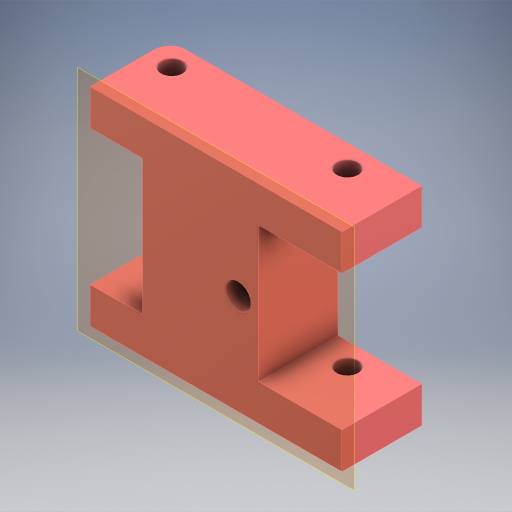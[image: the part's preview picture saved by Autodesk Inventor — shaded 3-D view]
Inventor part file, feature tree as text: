
AUTODESK INVENTOR PART (.ipt)
format: ipt  version: 2024 (Build 280153000, 153)  size: 279,552 bytes
history: native  units: in
note: dims shown in document units (in); Inventor stores cm internally (conversion verified against a paired STEP export)
features: other x4, extrude x2, sketch x2, reference x2, fillet x1
ambient origin geometry x8: Origin, YZ Plane, XZ Plane, XY Plane, X Axis, Y Axis, Z Axis, Center Point
bodies: Body1 (feature_tree)
feature tree (11):
  other  "솔리드1"
  other  "작업 평면2"
  extrude  "돌출1"  Depth=0.3937in TaperAngle=0.0deg
  extrude  "돌출2"  TaperAngle=0.0deg  [1 undecoded]
  fillet  "모깎기1"  Radius=0.0787in
  sketch  "스케치2"
  reference  "참조1"
  sketch  "스케치3"
  reference  "참조2"
  other  "조립품8"
  other  "foot_right_bottom_MIR_MIR_MIR:1"
note: 1 required parameter value undecoded (feature->parameter linkage not recoverable at this tier; creation-order binding heuristic only, values carry confidence <= 0.55)
